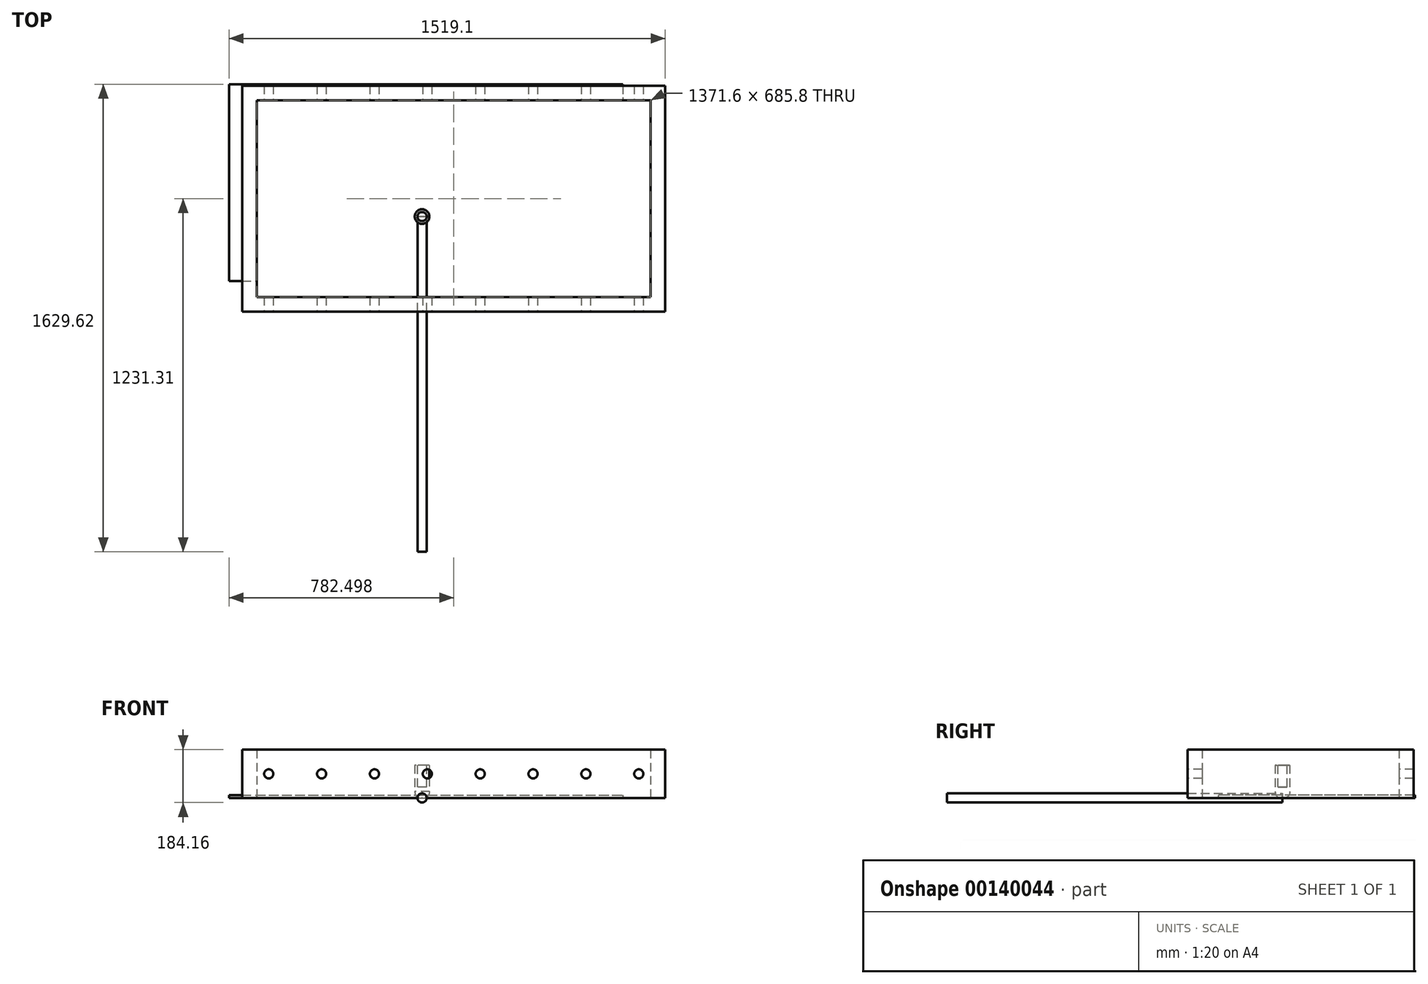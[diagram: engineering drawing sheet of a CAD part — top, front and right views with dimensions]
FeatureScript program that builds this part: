
annotation { "Feature Type Name" : "Feature", "Feature Type Description" : "" }
export const myFeature = defineFeature(function(context is Context, id is Id, definition is map)
    precondition{}
    {
        {
            var Q0;
            Q0=qCreatedBy(makeId("Top.planeOp"),FACE);
            var sketch = newSketch(context, id + "F0", { "sketchPlane" : qUnion([Q0])});
            skLineSegment(sketch, "E0.bottom", {"start": v(-672.21, 461.22) * mm, "end": v(699.39, 461.22) * mm});
            skLineSegment(sketch, "E0.top", {"start": v(-672.21, -224.58) * mm, "end": v(699.39, -224.58) * mm});
            skLineSegment(sketch, "E0.left", {"start": v(-672.21, 461.22) * mm, "end": v(-672.21, -224.58) * mm});
            skLineSegment(sketch, "E0.right", {"start": v(699.39, 461.22) * mm, "end": v(699.39, -224.58) * mm});
            skSolve(sketch);
        }
        {
            var Q0;
            Q0 = qSketchRegion(id + "F0", true);
            var Q1;
            Q1=makeQuery(id+"F0.imprint","IMPRINT",FACE,{"disambiguationData":[TD([[makeQuery(id+"F0.imprint","IMPRINT",EDGE,{"derivedFrom":sQuery(id+"F0.wireOp",EDGE,"E0.bottom")}),-1.0]])]});
            extrude(context, id + "F1", {"entities" : qUnion([Q0, Q1]), "depth" : 9.52 * mm});
        }
        {
            var Q0;
            Q0=qCreatedBy(makeId("Top.planeOp"),FACE);
            var sketch = newSketch(context, id + "F2", { "sketchPlane" : qUnion([Q0])});
            skLineSegment(sketch, "E1.bottom", {"start": v(-626.31, 456.6) * mm, "end": v(846.89, 456.6) * mm});
            skLineSegment(sketch, "E1.top", {"start": v(-626.31, -330.8) * mm, "end": v(846.89, -330.8) * mm});
            skLineSegment(sketch, "E1.left", {"start": v(-626.31, 456.6) * mm, "end": v(-626.31, -330.8) * mm});
            skLineSegment(sketch, "E1.right", {"start": v(846.89, 456.6) * mm, "end": v(846.89, -330.8) * mm});
            skSolve(sketch);
        }
        {
            var Q0;
            Q0=makeQuery(id+"F2.imprint","IMPRINT",FACE,{"disambiguationData":[TD([[makeQuery(id+"F2.imprint","IMPRINT",EDGE,{"derivedFrom":sQuery(id+"F2.wireOp",EDGE,"E1.bottom")}),-1.0]])]});
            extrude(context, id + "F3", {"entities" : qUnion([Q0]), "depth" : 168.27 * mm});
        }
        {
            var Q0;
            Q0=makeQuery(id+"F3.opExtrude","CAP_FACE",FACE,{"disambiguationData":[OSD([sQuery(id+"F2.wireOp",EDGE,"E1.bottom"),sQuery(id+"F2.wireOp",EDGE,"E1.top"),sQuery(id+"F2.wireOp",EDGE,"E1.left"),sQuery(id+"F2.wireOp",EDGE,"E1.right")])],"isStart":false});
            shell(context, id + "F4", {"entities" : qUnion([Q0]), "thickness" : 50.8 * mm});
        }
        {
            var Q0;
            Q0=makeQuery(id+"F4.opShell","OFFSET_FACE",FACE,{"disambiguationData":[OSD([sQuery(id+"F2.wireOp",EDGE,"E1.bottom"),sQuery(id+"F2.wireOp",EDGE,"E1.top"),sQuery(id+"F2.wireOp",EDGE,"E1.left"),sQuery(id+"F2.wireOp",EDGE,"E1.right")])]});
            extrude(context, id + "F5", {"entities" : qUnion([Q0]), "operationType" : NewBodyOperationType.REMOVE, "oppositeDirection" : true, "depth" : 127 * mm});
        }
        {
            var Q0;
            Q0=makeQuery(id+"F3.opExtrude","SWEPT_FACE",FACE,{"disambiguationData":[OSD([sQuery(id+"F2.wireOp",EDGE,"E1.top")])]});
            var sketch = newSketch(context, id + "F6", { "sketchPlane" : qUnion([Q0])});
            skCircle(sketch, "E2", {"center": v(-534.24, 84.14) * mm, "radius": 15.88 * mm});
            skPoint(sketch, "E2.centerSnap0", {"position": v(-626.31, 84.14) * mm});
            skLineSegment(sketch, "E3", {"start": v(-626.31, 84.14) * mm, "end": v(-550.11, 84.14) * mm});
            skLineSegment(sketch, "E4", {"start": v(-534.24, 84.14) * mm, "end": v(-350.09, 84.14) * mm});
            skCircle(sketch, "E5", {"center": v(-350.09, 84.14) * mm, "radius": 15.88 * mm});
            skLineSegment(sketch, "E6", {"start": v(-350.09, 84.14) * mm, "end": v(-165.94, 84.14) * mm});
            skCircle(sketch, "E7", {"center": v(-165.94, 84.14) * mm, "radius": 15.88 * mm});
            skLineSegment(sketch, "E8", {"start": v(-165.94, 84.14) * mm, "end": v(18.21, 84.14) * mm});
            skCircle(sketch, "E9", {"center": v(18.21, 84.14) * mm, "radius": 15.88 * mm});
            skLineSegment(sketch, "E10", {"start": v(18.21, 84.14) * mm, "end": v(202.36, 84.14) * mm});
            skCircle(sketch, "E11", {"center": v(202.36, 84.14) * mm, "radius": 15.88 * mm});
            skLineSegment(sketch, "E12", {"start": v(202.36, 84.14) * mm, "end": v(386.51, 84.14) * mm});
            skCircle(sketch, "E13", {"center": v(386.51, 84.14) * mm, "radius": 15.88 * mm});
            skLineSegment(sketch, "E14", {"start": v(386.51, 84.14) * mm, "end": v(570.66, 84.14) * mm});
            skCircle(sketch, "E15", {"center": v(570.66, 84.14) * mm, "radius": 15.88 * mm});
            skLineSegment(sketch, "E16", {"start": v(570.66, 84.14) * mm, "end": v(754.81, 84.14) * mm});
            skCircle(sketch, "E17", {"center": v(754.81, 84.14) * mm, "radius": 15.88 * mm});
            skLineSegment(sketch, "E18", {"start": v(754.81, 84.14) * mm, "end": v(846.89, 84.14) * mm});
            skSolve(sketch);
        }
        {
            var Q0;
            {var subQ0=sQuery(id+"F6.wireOp",EDGE,"E2");var subQ1=makeQuery(id+"F6.imprint","INTERSECT",VERTEX,{"derivedFrom":[subQ0,sQuery(id+"F6.wireOp",EDGE,"E3")]});Q0=makeQuery(id+"F6.imprint","IMPRINT",FACE,{"disambiguationData":[TD([[makeQuery(id+"F6.imprint","IMPRINT",EDGE,{"disambiguationData":[TD([[subQ1,1.0]])],"derivedFrom":subQ0}),1.0]])]});}
            var Q1;
            {var subQ0=sQuery(id+"F6.wireOp",EDGE,"E6");var subQ1=sQuery(id+"F6.wireOp",EDGE,"E4");var subQ2=makeQuery(id+"F6.imprint","INTERSECT",VERTEX,{"derivedFrom":[subQ1,subQ0]});Q1=makeQuery(id+"F6.imprint","IMPRINT",FACE,{"disambiguationData":[TD([[makeQuery(id+"F6.imprint","IMPRINT",EDGE,{"disambiguationData":[TD([[subQ2,1.0]])],"derivedFrom":subQ1}),1.0]])]});}
            var Q2;
            {var subQ0=sQuery(id+"F6.wireOp",EDGE,"E6");var subQ1=sQuery(id+"F6.wireOp",EDGE,"E4");var subQ2=makeQuery(id+"F6.imprint","INTERSECT",VERTEX,{"derivedFrom":[subQ1,subQ0]});Q2=makeQuery(id+"F6.imprint","IMPRINT",FACE,{"disambiguationData":[TD([[makeQuery(id+"F6.imprint","IMPRINT",EDGE,{"disambiguationData":[TD([[subQ2,1.0]])],"derivedFrom":subQ1}),-1.0]])]});}
            var Q3;
            {var subQ0=sQuery(id+"F6.wireOp",EDGE,"E8");var subQ1=sQuery(id+"F6.wireOp",EDGE,"E6");var subQ2=makeQuery(id+"F6.imprint","INTERSECT",VERTEX,{"derivedFrom":[subQ1,subQ0]});Q3=makeQuery(id+"F6.imprint","IMPRINT",FACE,{"disambiguationData":[TD([[makeQuery(id+"F6.imprint","IMPRINT",EDGE,{"disambiguationData":[TD([[subQ2,1.0]])],"derivedFrom":subQ1}),-1.0]])]});}
            var Q4;
            {var subQ0=sQuery(id+"F6.wireOp",EDGE,"E8");var subQ1=sQuery(id+"F6.wireOp",EDGE,"E6");var subQ2=makeQuery(id+"F6.imprint","INTERSECT",VERTEX,{"derivedFrom":[subQ1,subQ0]});Q4=makeQuery(id+"F6.imprint","IMPRINT",FACE,{"disambiguationData":[TD([[makeQuery(id+"F6.imprint","IMPRINT",EDGE,{"disambiguationData":[TD([[subQ2,1.0]])],"derivedFrom":subQ1}),1.0]])]});}
            var Q5;
            {var subQ0=sQuery(id+"F6.wireOp",EDGE,"E10");var subQ1=sQuery(id+"F6.wireOp",EDGE,"E8");var subQ2=makeQuery(id+"F6.imprint","INTERSECT",VERTEX,{"derivedFrom":[subQ1,subQ0]});Q5=makeQuery(id+"F6.imprint","IMPRINT",FACE,{"disambiguationData":[TD([[makeQuery(id+"F6.imprint","IMPRINT",EDGE,{"disambiguationData":[TD([[subQ2,1.0]])],"derivedFrom":subQ1}),-1.0]])]});}
            var Q6;
            {var subQ0=sQuery(id+"F6.wireOp",EDGE,"E10");var subQ1=sQuery(id+"F6.wireOp",EDGE,"E8");var subQ2=makeQuery(id+"F6.imprint","INTERSECT",VERTEX,{"derivedFrom":[subQ1,subQ0]});Q6=makeQuery(id+"F6.imprint","IMPRINT",FACE,{"disambiguationData":[TD([[makeQuery(id+"F6.imprint","IMPRINT",EDGE,{"disambiguationData":[TD([[subQ2,1.0]])],"derivedFrom":subQ1}),1.0]])]});}
            var Q7;
            {var subQ0=sQuery(id+"F6.wireOp",EDGE,"E12");var subQ1=sQuery(id+"F6.wireOp",EDGE,"E10");var subQ2=makeQuery(id+"F6.imprint","INTERSECT",VERTEX,{"derivedFrom":[subQ1,subQ0]});Q7=makeQuery(id+"F6.imprint","IMPRINT",FACE,{"disambiguationData":[TD([[makeQuery(id+"F6.imprint","IMPRINT",EDGE,{"disambiguationData":[TD([[subQ2,1.0]])],"derivedFrom":subQ1}),-1.0]])]});}
            var Q8;
            {var subQ0=sQuery(id+"F6.wireOp",EDGE,"E12");var subQ1=sQuery(id+"F6.wireOp",EDGE,"E10");var subQ2=makeQuery(id+"F6.imprint","INTERSECT",VERTEX,{"derivedFrom":[subQ1,subQ0]});Q8=makeQuery(id+"F6.imprint","IMPRINT",FACE,{"disambiguationData":[TD([[makeQuery(id+"F6.imprint","IMPRINT",EDGE,{"disambiguationData":[TD([[subQ2,1.0]])],"derivedFrom":subQ1}),1.0]])]});}
            var Q9;
            {var subQ0=sQuery(id+"F6.wireOp",EDGE,"E14");var subQ1=sQuery(id+"F6.wireOp",EDGE,"E12");var subQ2=makeQuery(id+"F6.imprint","INTERSECT",VERTEX,{"derivedFrom":[subQ1,subQ0]});Q9=makeQuery(id+"F6.imprint","IMPRINT",FACE,{"disambiguationData":[TD([[makeQuery(id+"F6.imprint","IMPRINT",EDGE,{"disambiguationData":[TD([[subQ2,1.0]])],"derivedFrom":subQ1}),-1.0]])]});}
            var Q10;
            {var subQ0=sQuery(id+"F6.wireOp",EDGE,"E14");var subQ1=sQuery(id+"F6.wireOp",EDGE,"E12");var subQ2=makeQuery(id+"F6.imprint","INTERSECT",VERTEX,{"derivedFrom":[subQ1,subQ0]});Q10=makeQuery(id+"F6.imprint","IMPRINT",FACE,{"disambiguationData":[TD([[makeQuery(id+"F6.imprint","IMPRINT",EDGE,{"disambiguationData":[TD([[subQ2,1.0]])],"derivedFrom":subQ1}),1.0]])]});}
            var Q11;
            {var subQ0=sQuery(id+"F6.wireOp",EDGE,"E16");var subQ1=sQuery(id+"F6.wireOp",EDGE,"E14");var subQ2=makeQuery(id+"F6.imprint","INTERSECT",VERTEX,{"derivedFrom":[subQ1,subQ0]});Q11=makeQuery(id+"F6.imprint","IMPRINT",FACE,{"disambiguationData":[TD([[makeQuery(id+"F6.imprint","IMPRINT",EDGE,{"disambiguationData":[TD([[subQ2,1.0]])],"derivedFrom":subQ1}),1.0]])]});}
            var Q12;
            {var subQ0=sQuery(id+"F6.wireOp",EDGE,"E16");var subQ1=sQuery(id+"F6.wireOp",EDGE,"E14");var subQ2=makeQuery(id+"F6.imprint","INTERSECT",VERTEX,{"derivedFrom":[subQ1,subQ0]});Q12=makeQuery(id+"F6.imprint","IMPRINT",FACE,{"disambiguationData":[TD([[makeQuery(id+"F6.imprint","IMPRINT",EDGE,{"disambiguationData":[TD([[subQ2,1.0]])],"derivedFrom":subQ1}),-1.0]])]});}
            var Q13;
            {var subQ0=sQuery(id+"F6.wireOp",EDGE,"E18");var subQ1=sQuery(id+"F6.wireOp",EDGE,"E16");var subQ2=makeQuery(id+"F6.imprint","INTERSECT",VERTEX,{"derivedFrom":[subQ1,subQ0]});Q13=makeQuery(id+"F6.imprint","IMPRINT",FACE,{"disambiguationData":[TD([[makeQuery(id+"F6.imprint","IMPRINT",EDGE,{"disambiguationData":[TD([[subQ2,1.0]])],"derivedFrom":subQ1}),-1.0]])]});}
            var Q14;
            {var subQ0=sQuery(id+"F6.wireOp",EDGE,"E18");var subQ1=sQuery(id+"F6.wireOp",EDGE,"E16");var subQ2=makeQuery(id+"F6.imprint","INTERSECT",VERTEX,{"derivedFrom":[subQ1,subQ0]});Q14=makeQuery(id+"F6.imprint","IMPRINT",FACE,{"disambiguationData":[TD([[makeQuery(id+"F6.imprint","IMPRINT",EDGE,{"disambiguationData":[TD([[subQ2,1.0]])],"derivedFrom":subQ1}),1.0]])]});}
            var Q15;
            Q15=sQuery(id+"F6.wireOp",EDGE,"E2");
            var Q16;
            Q16=sQuery(id+"F6.wireOp",EDGE,"E5");
            var Q17;
            Q17=sQuery(id+"F6.wireOp",EDGE,"E7");
            var Q18;
            Q18=sQuery(id+"F6.wireOp",EDGE,"E9");
            var Q19;
            Q19=sQuery(id+"F6.wireOp",EDGE,"E11");
            var Q20;
            Q20=sQuery(id+"F6.wireOp",EDGE,"E13");
            var Q21;
            Q21=sQuery(id+"F6.wireOp",EDGE,"E15");
            var Q22;
            Q22=sQuery(id+"F6.wireOp",EDGE,"E17");
            extrude(context, id + "F7", {"entities" : qUnion([Q0, Q1, Q2, Q3, Q4, Q5, Q6, Q7, Q8, Q9, Q10, Q11, Q12, Q13, Q14]), "operationType" : NewBodyOperationType.REMOVE, "surfaceEntities" : qUnion([Q15, Q16, Q17, Q18, Q19, Q20, Q21, Q22]), "oppositeDirection" : true, "depth" : 787.4 * mm});
        }
        {
            var Q0;
            Q0=qCreatedBy(makeId("Front.planeOp"),FACE);
            var sketch = newSketch(context, id + "F8", { "sketchPlane" : qUnion([Q0])});
            skCircle(sketch, "E19", {"center": v(0, 0) * mm, "radius": 15.88 * mm});
            skSolve(sketch);
        }
        {
            var Q0;
            Q0 = qSketchRegion(id + "F8", true);
            extrude(context, id + "F9", {"entities" : qUnion([Q0]), "depth" : 1168.4 * mm});
        }
        {
            var Q0;
            Q0=qCreatedBy(makeId("Top.planeOp"),FACE);
            var sketch = newSketch(context, id + "F10", { "sketchPlane" : qUnion([Q0])});
            skCircle(sketch, "E20", {"center": v(0, 0) * mm, "radius": 25.4 * mm});
            skSolve(sketch);
        }
        {
            var Q0;
            Q0 = qSketchRegion(id + "F10", true);
            extrude(context, id + "F11", {"entities" : qUnion([Q0]), "depth" : 114.3 * mm});
        }
        {
            var Q0;
            Q0=makeQuery(id+"F11.opExtrude","CAP_FACE",FACE,{"disambiguationData":[OSD([sQuery(id+"F10.wireOp",EDGE,"E20")])],"isStart":false});
            var sketch = newSketch(context, id + "F12", { "sketchPlane" : qUnion([Q0])});
            skCircle(sketch, "E21", {"center": v(0, 0) * mm, "radius": 15.88 * mm});
            skSolve(sketch);
        }
        {
            var Q0;
            Q0 = qSketchRegion(id + "F12", true);
            extrude(context, id + "F13", {"entities" : qUnion([Q0]), "operationType" : NewBodyOperationType.REMOVE, "oppositeDirection" : true, "depth" : 76.2 * mm});
        }
        {
            var Q0;
            Q0=makeQuery(id+"F11.opExtrude","CAP_EDGE",EDGE,{"disambiguationData":[OSD([sQuery(id+"F10.wireOp",EDGE,"E20")])],"isStart":true});
            fillet(context, id + "F14", {"entities" : qUnion([Q0]), "radius" : 22.86 * mm, "rho" : 0.5, "crossSection" : FilletCrossSection.CONIC, "allowEdgeOverflow" : false});
        }
    });
